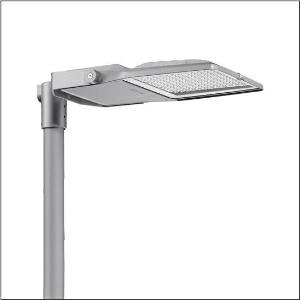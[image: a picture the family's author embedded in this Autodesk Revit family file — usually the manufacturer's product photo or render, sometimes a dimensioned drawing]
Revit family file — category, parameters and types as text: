
# Revit family: floodlight_fl_21_iq_midi___pl43_5xa7781f2a3a_7a49
name_source: partatom
category: Lighting Fixtures
units: mm (PartAtom-declared; Revit-internal decimal feet)

## family parameters
Cut with Voids When Loaded = No
Host = Face
Light Source = No
Part Type = Normal
Room Calculation Point = No
Round Connector Dimension = Use Diameter
Shared = No

## types (1)
- --- (1 x LED, 36680 lm, 270.2 W, 3000K)
    Apparent Load = 270 VA
    CIE Flux Codes = 27 78 99 100 100
    Color Rendering = 70
    Color Temperature = 3000K
    Default Elevation = 1800 mm
    Description = Floodlight FL 21 iQ midi, floodlight, primary light control with lens, of PMMA, primary optical cover: protective disc, of toughened safety glass, transparent, light distribution: PL43, light emission: direct distribution, installation type: surface-mounted, LED, High Power LED, rated luminous flux: 36.680lm, luminous efficacy: 136lm/W, light colour: 730, colour temperature: 3000K, control gear: ECG iQ, control: optimised constant luminous flux control (CLO 2.0), Desk-Remote (wireless, voltage-free reading and setting of iQ features in the workshop via application-optimized NFC function/RFID function), Light-Fading, Smart-Wire, Night-Set, Lumen-Switch, Temp-Guard, Auto-Match, with terminal, 6-pole, mains connection: 220..240V, AC, 50/60Hz, start of lifetime: 270W, end of service life: 287W, reduction: 117W, luminaire housing, of diecast aluminium, powder-coated, Siteco® metallic grey (DB 702S), corrosivity category C5 mid according to DIN EN ISO 12944, sealing non-destructively replaceable, please order mast flange separately, mast bracket, of steel, galvanised, powder-coated, Siteco® metallic grey (DB 702S), protection rating (complete): IP66, insulation class (complete): insulation class II (safety insulation), certification: CE, ENEC, VDE, protection symbol: D, impact resistance: IK08, permissible operating ambient temperature: -40..+40°C, permissible operating ambient temperature for outdoor applications: -40..+50°C, standard: DIN EN 12944, LABS conformity tested according to VDMA 24364:2018-05, packaging unit: 1 piece

Light Distribution: PL43
    Height = 76 mm
    Lamp = 1 x LED
    Lamp Light Flux = 36680 lm
    Lamp Power = 270.2 W
    Lamp count = 1
    Length = 657 mm
    Luminous efficacy = 136 lm/W
    Manufacturer = Siteco
    ModVariant = No
    Model = 5XA7781F2A3A
    Number of Poles = 1
    OnlyDefault = Yes
    Power Factor = 1
    Product Name = Floodlight FL 21 iQ midi | PL43
    Product group = floodlight | pylon annexe
    ProductGroupID = 6200
    Protection Class = Protection class II
    Protection Degree = IP 66
    RLX_Detail_Level = 1
    RLX_Emergency_Light_Flux = 0 lm
    RLX_Emergency_Type = 0
    RLX_Emergency_Type_DB = No
    RlxData = <blob elided: 153509 chars, md5=0c055a0c>
    Socket = socket
    Standby Power = 0 W
    System Light Flux = 36680 lm
    System Power = 270 W
    Type Comments = factory setting: luminous flux: 100 % | dim-lin: 254 | 620 mA
    Type Image = l_1007123.jpg
    URL = http://relux.com
    VarID = @adj_073735
    Voltage = 0 V
    Weight = 0.00 kg
    Width = 442 mm

## geometry (parser evidence)
native form markers: Blend x4, Sweep x14
no freeform markers — native parametric forms only
